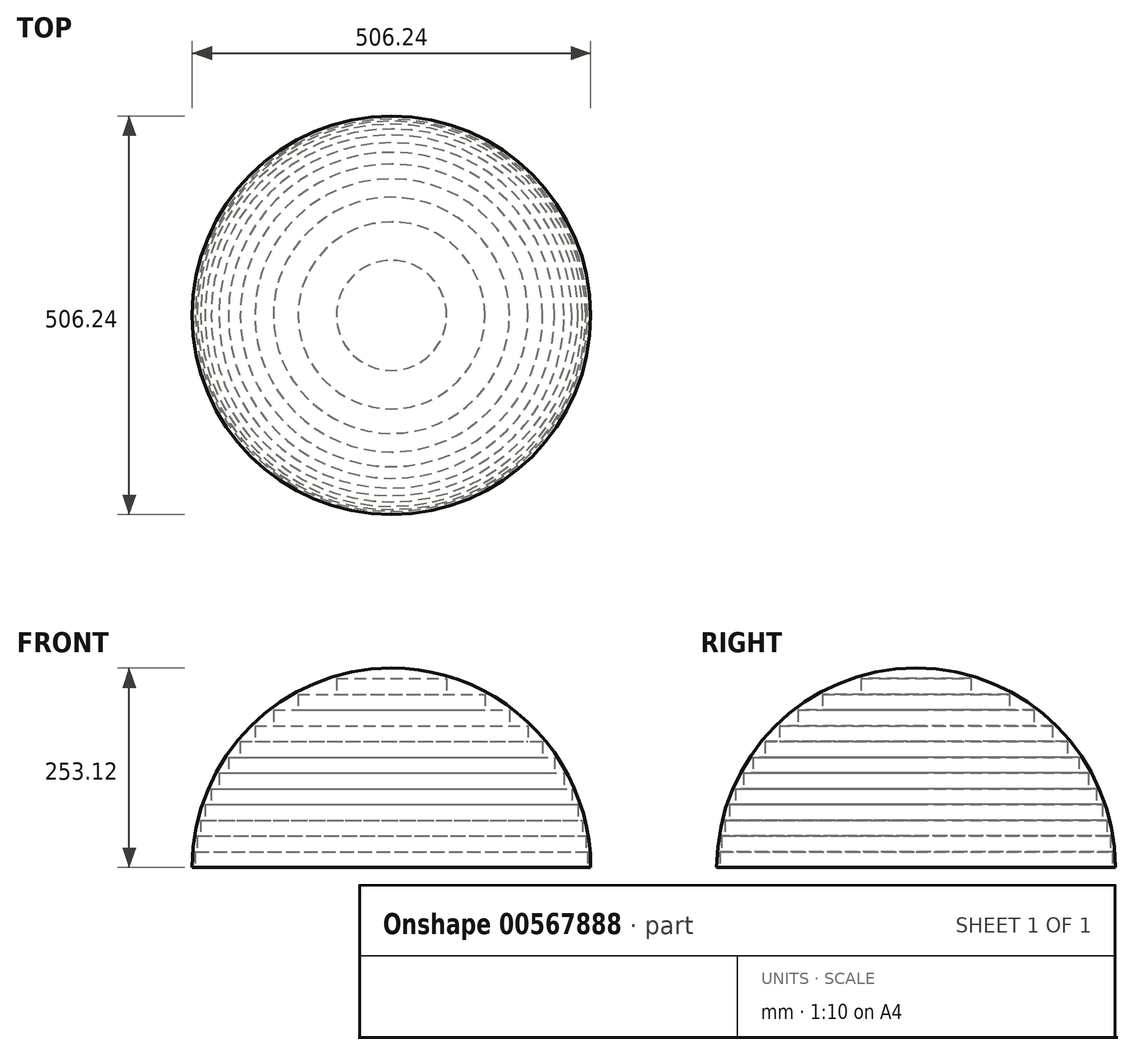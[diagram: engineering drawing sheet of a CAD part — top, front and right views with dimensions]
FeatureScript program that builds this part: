
annotation { "Feature Type Name" : "Feature", "Feature Type Description" : "" }
export const myFeature = defineFeature(function(context is Context, id is Id, definition is map)
    precondition{}
    {
        {
            var Q0;
            Q0=qCreatedBy(makeId("Front.planeOp"),FACE);
            var sketch = newSketch(context, id + "F0", { "sketchPlane" : qUnion([Q0])});
            skLineSegment(sketch, "E0.2.1.0", {"start": v(0, 20) * mm, "end": v(249.2, 20) * mm});
            skLineSegment(sketch, "E0.2.2.0", {"start": v(0, 40) * mm, "end": v(246.78, 40) * mm});
            skLineSegment(sketch, "E0.2.12.0", {"start": v(0, 240) * mm, "end": v(70, 240) * mm});
            skLineSegment(sketch, "E1", {"start": v(70, 240) * mm, "end": v(70, 220) * mm});
            skLineSegment(sketch, "E2", {"start": v(70, 220) * mm, "end": v(118.74, 220) * mm});
            skLineSegment(sketch, "E3", {"start": v(118.74, 220) * mm, "end": v(118.74, 200) * mm});
            skLineSegment(sketch, "E4", {"start": v(118.74, 200) * mm, "end": v(150, 200) * mm});
            skLineSegment(sketch, "E5", {"start": v(150, 200) * mm, "end": v(150, 180) * mm});
            skLineSegment(sketch, "E6", {"start": v(150, 180) * mm, "end": v(173.5, 180) * mm});
            skLineSegment(sketch, "E7", {"start": v(173.5, 180) * mm, "end": v(173.5, 160) * mm});
            skLineSegment(sketch, "E8", {"start": v(173.5, 160) * mm, "end": v(192.1, 160) * mm});
            skLineSegment(sketch, "E9", {"start": v(192.1, 160) * mm, "end": v(192.1, 140) * mm});
            skLineSegment(sketch, "E10", {"start": v(192.1, 140) * mm, "end": v(207.12, 140) * mm});
            skLineSegment(sketch, "E11", {"start": v(207.12, 140) * mm, "end": v(207.12, 120) * mm});
            skLineSegment(sketch, "E12", {"start": v(207.12, 120) * mm, "end": v(219.32, 120) * mm});
            skLineSegment(sketch, "E13", {"start": v(219.32, 120) * mm, "end": v(219.32, 100) * mm});
            skLineSegment(sketch, "E14", {"start": v(219.32, 100) * mm, "end": v(229.13, 100) * mm});
            skLineSegment(sketch, "E15", {"start": v(229.13, 100) * mm, "end": v(229.13, 80) * mm});
            skLineSegment(sketch, "E16", {"start": v(229.13, 80) * mm, "end": v(236.85, 80) * mm});
            skLineSegment(sketch, "E17", {"start": v(236.85, 80) * mm, "end": v(236.85, 60) * mm});
            skLineSegment(sketch, "E18", {"start": v(236.85, 60) * mm, "end": v(242.7, 60) * mm});
            skLineSegment(sketch, "E19", {"start": v(242.7, 40) * mm, "end": v(246.78, 40) * mm});
            skLineSegment(sketch, "E20", {"start": v(242.7, 60) * mm, "end": v(242.7, 40) * mm});
            skLineSegment(sketch, "E21", {"start": v(246.78, 40) * mm, "end": v(246.78, 20) * mm});
            skLineSegment(sketch, "E22", {"start": v(246.78, 20) * mm, "end": v(249.2, 20) * mm});
            skLineSegment(sketch, "E23", {"start": v(249.2, 20) * mm, "end": v(249.2, 0) * mm});
            skLineSegment(sketch, "E24", {"start": v(249.2, 0) * mm, "end": v(250, 0) * mm});
            skLineSegment(sketch, "E25", {"start": v(0, 0) * mm, "end": v(0, 240) * mm});
            skLineSegment(sketch, "E26.trimOffspring", {"start": v(0, 220) * mm, "end": v(118.74, 220) * mm});
            skLineSegment(sketch, "E27.trimOffspring", {"start": v(0, 200) * mm, "end": v(150, 200) * mm});
            skLineSegment(sketch, "E28.trimOffspring", {"start": v(0, 180) * mm, "end": v(173.5, 180) * mm});
            skLineSegment(sketch, "E29.trimOffspring", {"start": v(0, 160) * mm, "end": v(192.1, 160) * mm});
            skLineSegment(sketch, "E30.trimOffspring", {"start": v(0, 140) * mm, "end": v(207.12, 140) * mm});
            skLineSegment(sketch, "E31.trimOffspring", {"start": v(0, 120) * mm, "end": v(219.32, 120) * mm});
            skLineSegment(sketch, "E32.trimOffspring", {"start": v(0, 100) * mm, "end": v(229.13, 100) * mm});
            skLineSegment(sketch, "E33.trimOffspring", {"start": v(0, 80) * mm, "end": v(236.85, 80) * mm});
            skLineSegment(sketch, "E34.trimOffspring", {"start": v(0, 60) * mm, "end": v(242.7, 60) * mm});
            skLineSegment(sketch, "E35.trimOffspring", {"start": v(0, 0) * mm, "end": v(250, 0) * mm});
            skCircle(sketch, "E36", {"center": v(0, 0) * mm, "radius": 250 * mm});
            skSolve(sketch);
        }
        {
            var Q0;
            {var subQ0=sQuery(id+"F0.wireOp",EDGE,"E1");Q0=makeQuery(id+"F0.imprint","IMPRINT",FACE,{"disambiguationData":[TD([[makeQuery(id+"F0.imprint","IMPRINT",EDGE,{"derivedFrom":subQ0}),-1.0]])]});}
            var Q1;
            {var subQ5=sQuery(id+"F0.wireOp",EDGE,"E3");Q1=makeQuery(id+"F0.imprint","IMPRINT",FACE,{"disambiguationData":[TD([[makeQuery(id+"F0.imprint","IMPRINT",EDGE,{"derivedFrom":subQ5}),-1.0]])]});}
            var Q2;
            {var subQ5=sQuery(id+"F0.wireOp",EDGE,"E7");Q2=makeQuery(id+"F0.imprint","IMPRINT",FACE,{"disambiguationData":[TD([[makeQuery(id+"F0.imprint","IMPRINT",EDGE,{"derivedFrom":subQ5}),-1.0]])]});}
            var Q3;
            {var subQ5=sQuery(id+"F0.wireOp",EDGE,"E5");Q3=makeQuery(id+"F0.imprint","IMPRINT",FACE,{"disambiguationData":[TD([[makeQuery(id+"F0.imprint","IMPRINT",EDGE,{"derivedFrom":subQ5}),-1.0]])]});}
            var Q4;
            {var subQ2=sQuery(id+"F0.wireOp",EDGE,"E9");Q4=makeQuery(id+"F0.imprint","IMPRINT",FACE,{"disambiguationData":[TD([[makeQuery(id+"F0.imprint","IMPRINT",EDGE,{"derivedFrom":subQ2}),-1.0]])]});}
            var Q5;
            {var subQ4=sQuery(id+"F0.wireOp",EDGE,"E11");Q5=makeQuery(id+"F0.imprint","IMPRINT",FACE,{"disambiguationData":[TD([[makeQuery(id+"F0.imprint","IMPRINT",EDGE,{"derivedFrom":subQ4}),-1.0]])]});}
            var Q6;
            {var subQ2=sQuery(id+"F0.wireOp",EDGE,"E13");Q6=makeQuery(id+"F0.imprint","IMPRINT",FACE,{"disambiguationData":[TD([[makeQuery(id+"F0.imprint","IMPRINT",EDGE,{"derivedFrom":subQ2}),-1.0]])]});}
            var Q7;
            {var subQ6=sQuery(id+"F0.wireOp",EDGE,"E15");Q7=makeQuery(id+"F0.imprint","IMPRINT",FACE,{"disambiguationData":[TD([[makeQuery(id+"F0.imprint","IMPRINT",EDGE,{"derivedFrom":subQ6}),-1.0]])]});}
            var Q8;
            {var subQ2=sQuery(id+"F0.wireOp",EDGE,"E17");Q8=makeQuery(id+"F0.imprint","IMPRINT",FACE,{"disambiguationData":[TD([[makeQuery(id+"F0.imprint","IMPRINT",EDGE,{"derivedFrom":subQ2}),-1.0]])]});}
            var Q9;
            {var subQ2=sQuery(id+"F0.wireOp",EDGE,"E20");Q9=makeQuery(id+"F0.imprint","IMPRINT",FACE,{"disambiguationData":[TD([[makeQuery(id+"F0.imprint","IMPRINT",EDGE,{"derivedFrom":subQ2}),-1.0]])]});}
            var Q10;
            {var subQ4=sQuery(id+"F0.wireOp",EDGE,"E21");Q10=makeQuery(id+"F0.imprint","IMPRINT",FACE,{"disambiguationData":[TD([[makeQuery(id+"F0.imprint","IMPRINT",EDGE,{"derivedFrom":subQ4}),-1.0]])]});}
            var Q11;
            {var subQ2=sQuery(id+"F0.wireOp",EDGE,"E23");Q11=makeQuery(id+"F0.imprint","IMPRINT",FACE,{"disambiguationData":[TD([[makeQuery(id+"F0.imprint","IMPRINT",EDGE,{"derivedFrom":subQ2}),-1.0]])]});}
            var Q12;
            Q12=sQuery(id+"F0.wireOp",EDGE,"E25");
            revolve(context, id + "F1", {"entities" : qUnion([Q0, Q1, Q2, Q3, Q4, Q5, Q6, Q7, Q8, Q9, Q10, Q11]), "axis" : qUnion([Q12]), "revolveType" : RevolveType.FULL});
        }
        {
            var Q0;
            Q0=qCreatedBy(makeId("Front.planeOp"),FACE);
            var sketch = newSketch(context, id + "F2", { "sketchPlane" : qUnion([Q0])});
            skArc(sketch, "E37", {"start": v(253.12, 0) * mm, "mid": v(178.98, 178.98) * mm, "end": v(0, 253.12) * mm});
            skLineSegment(sketch, "E38", {"start": v(0, 0) * mm, "end": v(253.12, 0) * mm});
            skLineSegment(sketch, "E39", {"start": v(0, 253.12) * mm, "end": v(0, 0) * mm});
            skPoint(sketch, "E40.orphan", {"position": v(0, 285.3) * mm});
            skPoint(sketch, "E41.orphan", {"position": v(-275.42, 0) * mm});
            skSolve(sketch);
        }
        {
            var Q0;
            Q0=makeQuery(id+"F2.imprint","IMPRINT",FACE,{"disambiguationData":[TD([[makeQuery(id+"F2.imprint","IMPRINT",EDGE,{"derivedFrom":sQuery(id+"F2.wireOp",EDGE,"E37")}),1.0]])]});
            var Q1;
            Q1=sQuery(id+"F2.wireOp",EDGE,"E39");
            revolve(context, id + "F3", {"entities" : qUnion([Q0]), "axis" : qUnion([Q1]), "revolveType" : RevolveType.FULL});
        }
    });
